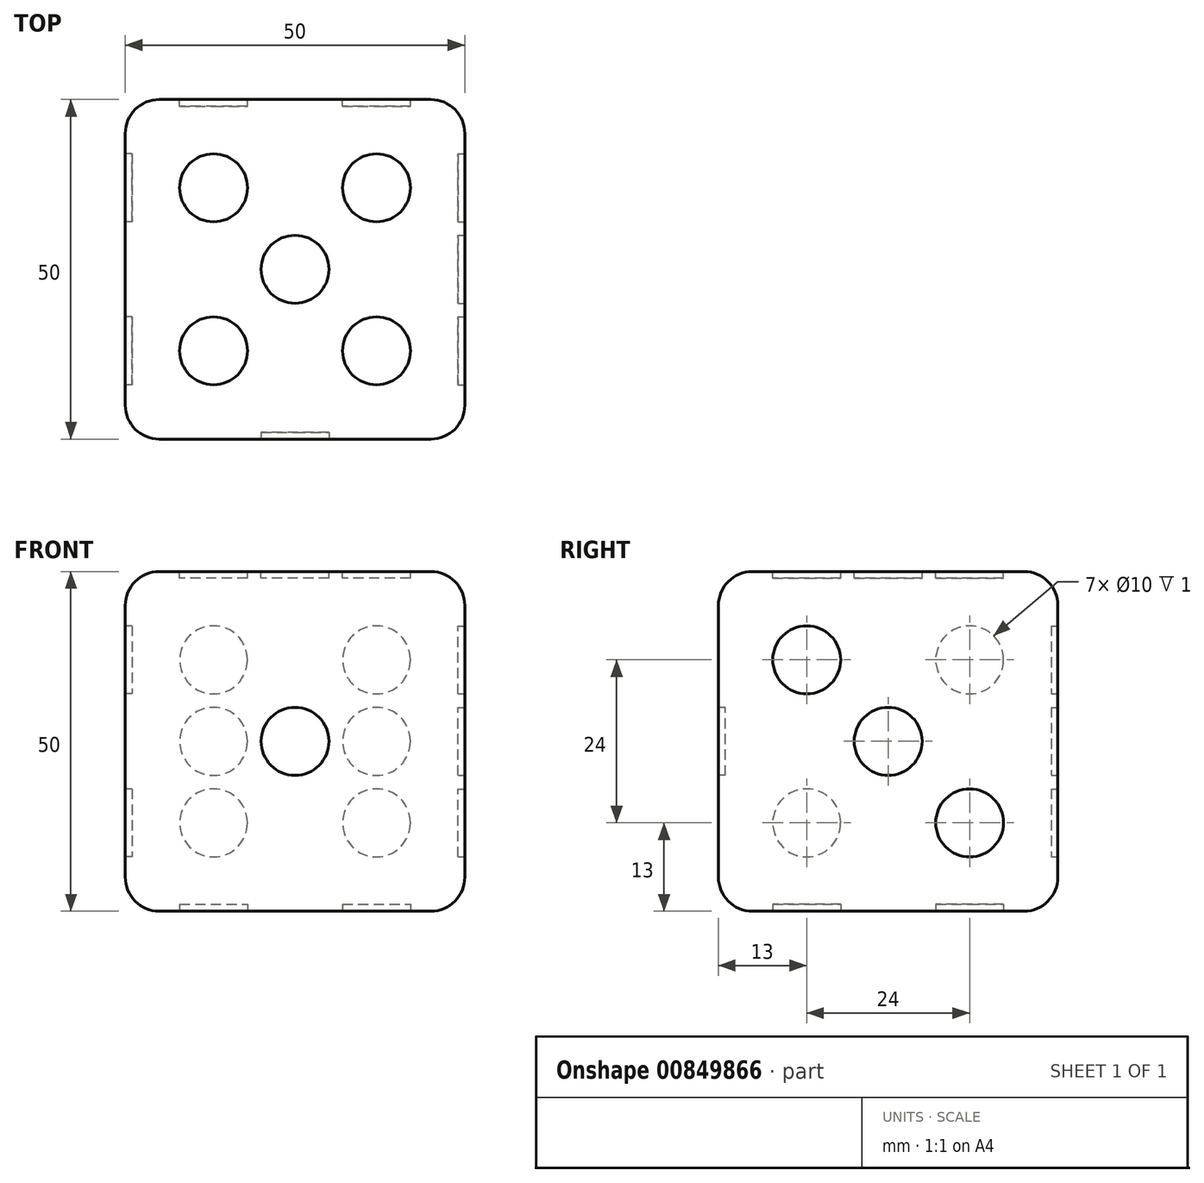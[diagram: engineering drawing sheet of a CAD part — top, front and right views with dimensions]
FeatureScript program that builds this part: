
annotation { "Feature Type Name" : "Feature", "Feature Type Description" : "" }
export const myFeature = defineFeature(function(context is Context, id is Id, definition is map)
    precondition{}
    {
        {
            var Q0;
            Q0=qCreatedBy(makeId("Front.planeOp"),FACE);
            var sketch = newSketch(context, id + "F0", { "sketchPlane" : qUnion([Q0])});
            skLineSegment(sketch, "E0.bottom", {"start": v(0, 0) * mm, "end": v(50, 0) * mm});
            skLineSegment(sketch, "E0.top", {"start": v(0, 50) * mm, "end": v(50, 50) * mm});
            skLineSegment(sketch, "E0.left", {"start": v(0, 0) * mm, "end": v(0, 50) * mm});
            skLineSegment(sketch, "E0.right", {"start": v(50, 0) * mm, "end": v(50, 50) * mm});
            skSolve(sketch);
        }
        {
            var Q0;
            Q0=qSketchRegion(id+"F0",true);
            extrude(context, id + "F1", {"entities" : qUnion([Q0]), "depth" : 50 * mm, "offsetDistance" : 25.4 * mm});
        }
        {
            var Q0;
            Q0=makeQuery(id+"F1.opExtrude","CAP_EDGE",EDGE,{"disambiguationData":[OSD([sQuery(id+"F0.wireOp",EDGE,"E0.right")])],"isStart":false});
            var Q1;
            Q1=makeQuery(id+"F1.opExtrude","SWEPT_EDGE",EDGE,{"disambiguationData":[OSD([sQuery(id+"F0.wireOp",EDGE,"E0.top"),sQuery(id+"F0.wireOp",EDGE,"E0.right")])]});
            var Q2;
            Q2=makeQuery(id+"F1.opExtrude","CAP_EDGE",EDGE,{"disambiguationData":[OSD([sQuery(id+"F0.wireOp",EDGE,"E0.top")])],"isStart":false});
            var Q3;
            Q3=makeQuery(id+"F1.opExtrude","CAP_EDGE",EDGE,{"disambiguationData":[OSD([sQuery(id+"F0.wireOp",EDGE,"E0.bottom")])],"isStart":false});
            var Q4;
            Q4=makeQuery(id+"F1.opExtrude","SWEPT_EDGE",EDGE,{"disambiguationData":[OSD([sQuery(id+"F0.wireOp",EDGE,"E0.bottom"),sQuery(id+"F0.wireOp",EDGE,"E0.right")])]});
            var Q5;
            Q5=makeQuery(id+"F1.opExtrude","CAP_EDGE",EDGE,{"disambiguationData":[OSD([sQuery(id+"F0.wireOp",EDGE,"E0.right")])],"isStart":true});
            var Q6;
            Q6=makeQuery(id+"F1.opExtrude","CAP_EDGE",EDGE,{"disambiguationData":[OSD([sQuery(id+"F0.wireOp",EDGE,"E0.top")])],"isStart":true});
            var Q7;
            Q7=makeQuery(id+"F1.opExtrude","SWEPT_EDGE",EDGE,{"disambiguationData":[OSD([sQuery(id+"F0.wireOp",EDGE,"E0.top"),sQuery(id+"F0.wireOp",EDGE,"E0.left")])]});
            var Q8;
            Q8=makeQuery(id+"F1.opExtrude","CAP_EDGE",EDGE,{"disambiguationData":[OSD([sQuery(id+"F0.wireOp",EDGE,"E0.left")])],"isStart":true});
            var Q9;
            Q9=makeQuery(id+"F1.opExtrude","CAP_EDGE",EDGE,{"disambiguationData":[OSD([sQuery(id+"F0.wireOp",EDGE,"E0.bottom")])],"isStart":true});
            var Q10;
            Q10=makeQuery(id+"F1.opExtrude","SWEPT_EDGE",EDGE,{"disambiguationData":[OSD([sQuery(id+"F0.wireOp",EDGE,"E0.bottom"),sQuery(id+"F0.wireOp",EDGE,"E0.left")])]});
            var Q11;
            Q11=makeQuery(id+"F1.opExtrude","CAP_EDGE",EDGE,{"disambiguationData":[OSD([sQuery(id+"F0.wireOp",EDGE,"E0.left")])],"isStart":false});
            fillet(context, id + "F2", {"entities" : qUnion([Q0, Q1, Q2, Q3, Q4, Q5, Q6, Q7, Q8, Q9, Q10, Q11]), "radius" : 5 * mm, "tangentPropagation" : true, "allowEdgeOverflow" : false});
        }
        {
            var Q0;
            Q0=makeQuery(id+"F1.opExtrude","CAP_FACE",FACE,{"disambiguationData":[OSD([sQuery(id+"F0.wireOp",EDGE,"E0.bottom"),sQuery(id+"F0.wireOp",EDGE,"E0.top"),sQuery(id+"F0.wireOp",EDGE,"E0.left"),sQuery(id+"F0.wireOp",EDGE,"E0.right")])],"isStart":false});
            var sketch = newSketch(context, id + "F3", { "sketchPlane" : qUnion([Q0])});
            skLineSegment(sketch, "E1", {"start": v(5, 45) * mm, "end": v(45, 45) * mm, "construction": true});
            skLineSegment(sketch, "E2", {"start": v(25, 45) * mm, "end": v(25, 5) * mm, "construction": true});
            skCircle(sketch, "E3", {"center": v(25, 25) * mm, "radius": 5 * mm});
            skSolve(sketch);
        }
        {
            var Q0;
            Q0=qSketchRegion(id+"F3",true);
            extrude(context, id + "F4", {"entities" : qUnion([Q0]), "operationType" : NewBodyOperationType.REMOVE, "oppositeDirection" : true, "depth" : 1 * mm, "offsetDistance" : 25.4 * mm});
        }
        {
            var Q0;
            Q0=makeQuery(id+"F1.opExtrude","CAP_FACE",FACE,{"disambiguationData":[OSD([sQuery(id+"F0.wireOp",EDGE,"E0.bottom"),sQuery(id+"F0.wireOp",EDGE,"E0.top"),sQuery(id+"F0.wireOp",EDGE,"E0.left"),sQuery(id+"F0.wireOp",EDGE,"E0.right")])],"isStart":true});
            var sketch = newSketch(context, id + "F5", { "sketchPlane" : qUnion([Q0])});
            skLineSegment(sketch, "E4.bottom", {"start": v(-45, 45) * mm, "end": v(-5, 45) * mm, "construction": true});
            skLineSegment(sketch, "E4.top", {"start": v(-45, 37) * mm, "end": v(-5, 37) * mm, "construction": true});
            skLineSegment(sketch, "E4.left", {"start": v(-45, 45) * mm, "end": v(-45, 37) * mm, "construction": true});
            skLineSegment(sketch, "E4.right", {"start": v(-5, 45) * mm, "end": v(-5, 37) * mm, "construction": true});
            skLineSegment(sketch, "E5.bottom", {"start": v(-45, 5) * mm, "end": v(-5, 5) * mm, "construction": true});
            skLineSegment(sketch, "E5.top", {"start": v(-45, 13) * mm, "end": v(-5, 13) * mm, "construction": true});
            skLineSegment(sketch, "E5.left", {"start": v(-45, 5) * mm, "end": v(-45, 13) * mm, "construction": true});
            skLineSegment(sketch, "E5.right", {"start": v(-5, 5) * mm, "end": v(-5, 13) * mm, "construction": true});
            skLineSegment(sketch, "E6", {"start": v(-45, 25) * mm, "end": v(-37, 25) * mm, "construction": true});
            skLineSegment(sketch, "E7", {"start": v(-37, 25) * mm, "end": v(-13, 25) * mm, "construction": true});
            skLineSegment(sketch, "E8", {"start": v(-13, 25) * mm, "end": v(-5, 25) * mm, "construction": true});
            skLineSegment(sketch, "E9", {"start": v(-37, 37) * mm, "end": v(-37, 25) * mm, "construction": true});
            skLineSegment(sketch, "E10", {"start": v(-37, 13) * mm, "end": v(-37, 25) * mm, "construction": true});
            skLineSegment(sketch, "E11", {"start": v(-13, 37) * mm, "end": v(-13, 25) * mm, "construction": true});
            skLineSegment(sketch, "E12", {"start": v(-13, 13) * mm, "end": v(-13, 25) * mm, "construction": true});
            skCircle(sketch, "E13", {"center": v(-37, 37) * mm, "radius": 5 * mm});
            skCircle(sketch, "E14", {"center": v(-13, 37) * mm, "radius": 5 * mm});
            skCircle(sketch, "E15", {"center": v(-37, 25) * mm, "radius": 5 * mm});
            skCircle(sketch, "E16", {"center": v(-13, 25) * mm, "radius": 5 * mm});
            skCircle(sketch, "E17", {"center": v(-37, 13) * mm, "radius": 5 * mm});
            skCircle(sketch, "E18", {"center": v(-13, 13) * mm, "radius": 5 * mm});
            skSolve(sketch);
        }
        {
            var Q0;
            Q0=makeQuery(id+"F5.imprint","IMPRINT",FACE,{"disambiguationData":[TD([[makeQuery(id+"F5.imprint","IMPRINT",EDGE,{"derivedFrom":sQuery(id+"F5.wireOp",EDGE,"E13")}),1.0]])]});
            var Q1;
            Q1=makeQuery(id+"F5.imprint","IMPRINT",FACE,{"disambiguationData":[TD([[makeQuery(id+"F5.imprint","IMPRINT",EDGE,{"derivedFrom":sQuery(id+"F5.wireOp",EDGE,"E14")}),1.0]])]});
            var Q2;
            Q2=makeQuery(id+"F5.imprint","IMPRINT",FACE,{"disambiguationData":[TD([[makeQuery(id+"F5.imprint","IMPRINT",EDGE,{"derivedFrom":sQuery(id+"F5.wireOp",EDGE,"E15")}),1.0]])]});
            var Q3;
            Q3=makeQuery(id+"F5.imprint","IMPRINT",FACE,{"disambiguationData":[TD([[makeQuery(id+"F5.imprint","IMPRINT",EDGE,{"derivedFrom":sQuery(id+"F5.wireOp",EDGE,"E16")}),1.0]])]});
            var Q4;
            Q4=makeQuery(id+"F5.imprint","IMPRINT",FACE,{"disambiguationData":[TD([[makeQuery(id+"F5.imprint","IMPRINT",EDGE,{"derivedFrom":sQuery(id+"F5.wireOp",EDGE,"E18")}),1.0]])]});
            var Q5;
            Q5=makeQuery(id+"F5.imprint","IMPRINT",FACE,{"disambiguationData":[TD([[makeQuery(id+"F5.imprint","IMPRINT",EDGE,{"derivedFrom":sQuery(id+"F5.wireOp",EDGE,"E17")}),1.0]])]});
            extrude(context, id + "F6", {"entities" : qUnion([Q0, Q1, Q2, Q3, Q4, Q5]), "operationType" : NewBodyOperationType.REMOVE, "oppositeDirection" : true, "depth" : 1 * mm, "offsetDistance" : 25.4 * mm});
        }
        {
            var Q0;
            Q0=makeQuery(id+"F1.opExtrude","SWEPT_FACE",FACE,{"disambiguationData":[OSD([sQuery(id+"F0.wireOp",EDGE,"E0.top")])]});
            var sketch = newSketch(context, id + "F7", { "sketchPlane" : qUnion([Q0])});
            skLineSegment(sketch, "E19", {"start": v(45, -5) * mm, "end": v(5, -45) * mm, "construction": true});
            skLineSegment(sketch, "E20", {"start": v(5, -45) * mm, "end": v(45, -45) * mm, "construction": true});
            skLineSegment(sketch, "E21", {"start": v(45, -45) * mm, "end": v(45, -5) * mm, "construction": true});
            skLineSegment(sketch, "E22", {"start": v(5, -5) * mm, "end": v(5, -45) * mm, "construction": true});
            skLineSegment(sketch, "E23", {"start": v(45, -45) * mm, "end": v(5, -5) * mm, "construction": true});
            skLineSegment(sketch, "E24", {"start": v(45, -5) * mm, "end": v(5, -5) * mm, "construction": true});
            skLineSegment(sketch, "E25", {"start": v(45, -37) * mm, "end": v(5, -37) * mm, "construction": true});
            skLineSegment(sketch, "E26", {"start": v(45, -13) * mm, "end": v(5, -13) * mm, "construction": true});
            skLineSegment(sketch, "E27", {"start": v(25, -37) * mm, "end": v(25, -45) * mm, "construction": true});
            skLineSegment(sketch, "E28", {"start": v(25, -5) * mm, "end": v(25, -13) * mm, "construction": true});
            skCircle(sketch, "E29", {"center": v(37, -13) * mm, "radius": 5 * mm});
            skCircle(sketch, "E30", {"center": v(37, -37) * mm, "radius": 5 * mm});
            skCircle(sketch, "E31", {"center": v(25, -25) * mm, "radius": 5 * mm});
            skCircle(sketch, "E32", {"center": v(13, -13) * mm, "radius": 5 * mm});
            skCircle(sketch, "E33", {"center": v(13, -37) * mm, "radius": 5 * mm});
            skSolve(sketch);
        }
        {
            var Q0;
            Q0=makeQuery(id+"F7.imprint","IMPRINT",FACE,{"disambiguationData":[TD([[makeQuery(id+"F7.imprint","IMPRINT",EDGE,{"derivedFrom":sQuery(id+"F7.wireOp",EDGE,"E29")}),1.0]])]});
            var Q1;
            Q1=makeQuery(id+"F7.imprint","IMPRINT",FACE,{"disambiguationData":[TD([[makeQuery(id+"F7.imprint","IMPRINT",EDGE,{"derivedFrom":sQuery(id+"F7.wireOp",EDGE,"E30")}),1.0]])]});
            var Q2;
            Q2=makeQuery(id+"F7.imprint","IMPRINT",FACE,{"disambiguationData":[TD([[makeQuery(id+"F7.imprint","IMPRINT",EDGE,{"derivedFrom":sQuery(id+"F7.wireOp",EDGE,"E31")}),1.0]])]});
            var Q3;
            Q3=makeQuery(id+"F7.imprint","IMPRINT",FACE,{"disambiguationData":[TD([[makeQuery(id+"F7.imprint","IMPRINT",EDGE,{"derivedFrom":sQuery(id+"F7.wireOp",EDGE,"E32")}),1.0]])]});
            var Q4;
            Q4=makeQuery(id+"F7.imprint","IMPRINT",FACE,{"disambiguationData":[TD([[makeQuery(id+"F7.imprint","IMPRINT",EDGE,{"derivedFrom":sQuery(id+"F7.wireOp",EDGE,"E33")}),1.0]])]});
            extrude(context, id + "F8", {"entities" : qUnion([Q0, Q1, Q2, Q3, Q4]), "operationType" : NewBodyOperationType.REMOVE, "oppositeDirection" : true, "depth" : 1 * mm, "offsetDistance" : 25.4 * mm});
        }
        {
            var Q0;
            Q0=makeQuery(id+"F1.opExtrude","SWEPT_FACE",FACE,{"disambiguationData":[OSD([sQuery(id+"F0.wireOp",EDGE,"E0.bottom")])]});
            var sketch = newSketch(context, id + "F9", { "sketchPlane" : qUnion([Q0])});
            skLineSegment(sketch, "E34", {"start": v(45, 45) * mm, "end": v(5, 5) * mm, "construction": true});
            skLineSegment(sketch, "E35", {"start": v(45, 37) * mm, "end": v(5, 37) * mm, "construction": true});
            skLineSegment(sketch, "E36", {"start": v(45, 13) * mm, "end": v(5, 13) * mm, "construction": true});
            skCircle(sketch, "E37", {"center": v(37, 37) * mm, "radius": 5 * mm});
            skCircle(sketch, "E38", {"center": v(13, 13) * mm, "radius": 5 * mm});
            skSolve(sketch);
        }
        {
            var Q0;
            Q0=makeQuery(id+"F9.imprint","IMPRINT",FACE,{"disambiguationData":[TD([[makeQuery(id+"F9.imprint","IMPRINT",EDGE,{"derivedFrom":sQuery(id+"F9.wireOp",EDGE,"E37")}),1.0]])]});
            var Q1;
            Q1=makeQuery(id+"F9.imprint","IMPRINT",FACE,{"disambiguationData":[TD([[makeQuery(id+"F9.imprint","IMPRINT",EDGE,{"derivedFrom":sQuery(id+"F9.wireOp",EDGE,"E38")}),1.0]])]});
            extrude(context, id + "F10", {"entities" : qUnion([Q0, Q1]), "operationType" : NewBodyOperationType.REMOVE, "oppositeDirection" : true, "depth" : 1 * mm, "offsetDistance" : 25.4 * mm});
        }
        {
            var Q0;
            Q0=makeQuery(id+"F1.opExtrude","SWEPT_FACE",FACE,{"disambiguationData":[OSD([sQuery(id+"F0.wireOp",EDGE,"E0.right")])]});
            var sketch = newSketch(context, id + "F11", { "sketchPlane" : qUnion([Q0])});
            skLineSegment(sketch, "E39", {"start": v(-5, 5) * mm, "end": v(-45, 45) * mm, "construction": true});
            skLineSegment(sketch, "E40", {"start": v(-45, 37) * mm, "end": v(-5, 37) * mm, "construction": true});
            skLineSegment(sketch, "E41", {"start": v(-45, 13) * mm, "end": v(-5, 13) * mm, "construction": true});
            skCircle(sketch, "E42", {"center": v(-13, 13) * mm, "radius": 5 * mm});
            skCircle(sketch, "E43", {"center": v(-25, 25) * mm, "radius": 5 * mm});
            skCircle(sketch, "E44", {"center": v(-37, 37) * mm, "radius": 5 * mm});
            skSolve(sketch);
        }
        {
            var Q0;
            Q0=makeQuery(id+"F11.imprint","IMPRINT",FACE,{"disambiguationData":[TD([[makeQuery(id+"F11.imprint","IMPRINT",EDGE,{"derivedFrom":sQuery(id+"F11.wireOp",EDGE,"E44")}),1.0]])]});
            var Q1;
            Q1=makeQuery(id+"F11.imprint","IMPRINT",FACE,{"disambiguationData":[TD([[makeQuery(id+"F11.imprint","IMPRINT",EDGE,{"derivedFrom":sQuery(id+"F11.wireOp",EDGE,"E43")}),1.0]])]});
            var Q2;
            Q2=makeQuery(id+"F11.imprint","IMPRINT",FACE,{"disambiguationData":[TD([[makeQuery(id+"F11.imprint","IMPRINT",EDGE,{"derivedFrom":sQuery(id+"F11.wireOp",EDGE,"E42")}),1.0]])]});
            extrude(context, id + "F12", {"entities" : qUnion([Q0, Q1, Q2]), "operationType" : NewBodyOperationType.REMOVE, "oppositeDirection" : true, "depth" : 1 * mm, "offsetDistance" : 25.4 * mm});
        }
        {
            var Q0;
            Q0=makeQuery(id+"F1.opExtrude","SWEPT_FACE",FACE,{"disambiguationData":[OSD([sQuery(id+"F0.wireOp",EDGE,"E0.left")])]});
            var sketch = newSketch(context, id + "F13", { "sketchPlane" : qUnion([Q0])});
            skLineSegment(sketch, "E45", {"start": v(5, 45) * mm, "end": v(45, 5) * mm, "construction": true});
            skLineSegment(sketch, "E46", {"start": v(45, 5) * mm, "end": v(45, 45) * mm, "construction": true});
            skLineSegment(sketch, "E47", {"start": v(45, 45) * mm, "end": v(5, 5) * mm, "construction": true});
            skLineSegment(sketch, "E48", {"start": v(45, 13) * mm, "end": v(5, 13) * mm, "construction": true});
            skLineSegment(sketch, "E49", {"start": v(45, 37) * mm, "end": v(5, 37) * mm, "construction": true});
            skLineSegment(sketch, "E50", {"start": v(25, 45) * mm, "end": v(25, 37) * mm, "construction": true});
            skLineSegment(sketch, "E51", {"start": v(25, 13) * mm, "end": v(25, 5) * mm, "construction": true});
            skCircle(sketch, "E52", {"center": v(37, 37) * mm, "radius": 5 * mm});
            skCircle(sketch, "E53", {"center": v(37, 13) * mm, "radius": 5 * mm});
            skCircle(sketch, "E54", {"center": v(13, 13) * mm, "radius": 5 * mm});
            skCircle(sketch, "E55", {"center": v(13, 37) * mm, "radius": 5 * mm});
            skSolve(sketch);
        }
        {
            var Q0;
            Q0=makeQuery(id+"F13.imprint","IMPRINT",FACE,{"disambiguationData":[TD([[makeQuery(id+"F13.imprint","IMPRINT",EDGE,{"derivedFrom":sQuery(id+"F13.wireOp",EDGE,"E52")}),1.0]])]});
            var Q1;
            Q1=makeQuery(id+"F13.imprint","IMPRINT",FACE,{"disambiguationData":[TD([[makeQuery(id+"F13.imprint","IMPRINT",EDGE,{"derivedFrom":sQuery(id+"F13.wireOp",EDGE,"E53")}),1.0]])]});
            var Q2;
            Q2=makeQuery(id+"F13.imprint","IMPRINT",FACE,{"disambiguationData":[TD([[makeQuery(id+"F13.imprint","IMPRINT",EDGE,{"derivedFrom":sQuery(id+"F13.wireOp",EDGE,"E54")}),1.0]])]});
            var Q3;
            Q3=makeQuery(id+"F13.imprint","IMPRINT",FACE,{"disambiguationData":[TD([[makeQuery(id+"F13.imprint","IMPRINT",EDGE,{"derivedFrom":sQuery(id+"F13.wireOp",EDGE,"E55")}),1.0]])]});
            extrude(context, id + "F14", {"entities" : qUnion([Q0, Q1, Q2, Q3]), "operationType" : NewBodyOperationType.REMOVE, "oppositeDirection" : true, "depth" : 1 * mm, "offsetDistance" : 25.4 * mm});
        }
    });
